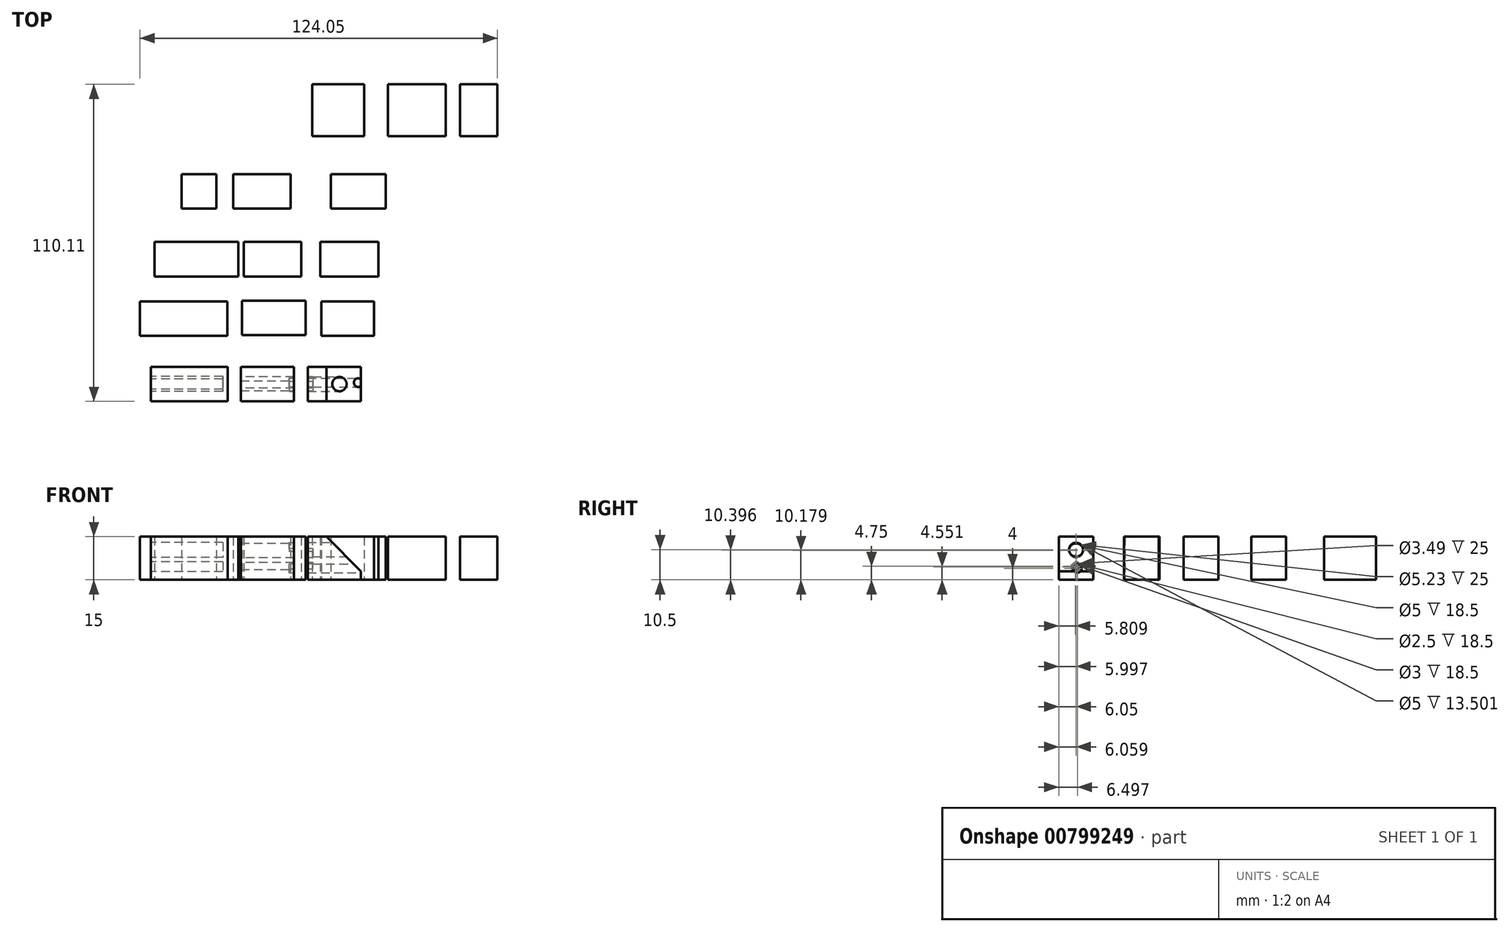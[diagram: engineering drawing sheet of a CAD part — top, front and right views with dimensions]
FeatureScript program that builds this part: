
annotation { "Feature Type Name" : "Feature", "Feature Type Description" : "" }
export const myFeature = defineFeature(function(context is Context, id is Id, definition is map)
    precondition{}
    {
        {
            var Q0;
            Q0=qCreatedBy(makeId("Top.planeOp"),FACE);
            var sketch = newSketch(context, id + "F0", { "sketchPlane" : qUnion([Q0])});
            skLineSegment(sketch, "E0.bottom", {"start": v(-47.12, -60.81) * mm, "end": v(-20.37, -60.81) * mm});
            skLineSegment(sketch, "E0.top", {"start": v(-47.12, -48.81) * mm, "end": v(-20.37, -48.81) * mm});
            skLineSegment(sketch, "E0.left", {"start": v(-47.12, -60.81) * mm, "end": v(-47.12, -48.81) * mm});
            skLineSegment(sketch, "E0.right", {"start": v(-20.37, -60.81) * mm, "end": v(-20.37, -48.81) * mm});
            skLineSegment(sketch, "E1.bottom", {"start": v(-15.87, -60.81) * mm, "end": v(2.63, -60.81) * mm});
            skLineSegment(sketch, "E1.top", {"start": v(-15.87, -48.81) * mm, "end": v(2.63, -48.81) * mm});
            skLineSegment(sketch, "E1.left", {"start": v(-15.87, -60.81) * mm, "end": v(-15.87, -48.81) * mm});
            skLineSegment(sketch, "E1.right", {"start": v(2.63, -60.81) * mm, "end": v(2.63, -48.81) * mm});
            skLineSegment(sketch, "E2.bottom", {"start": v(7.38, -48.81) * mm, "end": v(25.88, -48.81) * mm});
            skLineSegment(sketch, "E2.top", {"start": v(7.38, -60.81) * mm, "end": v(25.88, -60.81) * mm});
            skLineSegment(sketch, "E2.left", {"start": v(7.38, -48.81) * mm, "end": v(7.38, -60.81) * mm});
            skLineSegment(sketch, "E2.right", {"start": v(25.88, -48.81) * mm, "end": v(25.88, -60.81) * mm});
            skLineSegment(sketch, "E3.bottom", {"start": v(-20.54, -38.1) * mm, "end": v(-50.85, -38.1) * mm});
            skLineSegment(sketch, "E3.top", {"start": v(-20.54, -26.1) * mm, "end": v(-50.85, -26.1) * mm});
            skLineSegment(sketch, "E3.left", {"start": v(-20.54, -38.1) * mm, "end": v(-20.54, -26.1) * mm});
            skLineSegment(sketch, "E3.right", {"start": v(-50.85, -38.1) * mm, "end": v(-50.85, -26.1) * mm});
            skLineSegment(sketch, "E4.bottom", {"start": v(-15.44, -37.82) * mm, "end": v(6.66, -37.82) * mm});
            skLineSegment(sketch, "E4.top", {"start": v(-15.44, -25.82) * mm, "end": v(6.66, -25.82) * mm});
            skLineSegment(sketch, "E4.left", {"start": v(-15.44, -37.82) * mm, "end": v(-15.44, -25.82) * mm});
            skLineSegment(sketch, "E4.right", {"start": v(6.66, -37.82) * mm, "end": v(6.66, -25.82) * mm});
            skLineSegment(sketch, "E5.bottom", {"start": v(12.04, -38.1) * mm, "end": v(30.45, -38.1) * mm});
            skLineSegment(sketch, "E5.top", {"start": v(12.04, -26.1) * mm, "end": v(30.45, -26.1) * mm});
            skLineSegment(sketch, "E5.left", {"start": v(12.04, -38.1) * mm, "end": v(12.04, -26.1) * mm});
            skLineSegment(sketch, "E5.right", {"start": v(30.45, -38.1) * mm, "end": v(30.45, -26.1) * mm});
            skLineSegment(sketch, "E6.bottom", {"start": v(-45.75, -17.42) * mm, "end": v(-16.75, -17.42) * mm});
            skLineSegment(sketch, "E6.top", {"start": v(-45.75, -5.42) * mm, "end": v(-16.75, -5.42) * mm});
            skLineSegment(sketch, "E6.left", {"start": v(-45.75, -17.42) * mm, "end": v(-45.75, -5.42) * mm});
            skLineSegment(sketch, "E6.right", {"start": v(-16.75, -17.42) * mm, "end": v(-16.75, -5.42) * mm});
            skLineSegment(sketch, "E7.bottom", {"start": v(-14.87, -17.42) * mm, "end": v(5.13, -17.42) * mm});
            skLineSegment(sketch, "E7.top", {"start": v(-14.87, -5.42) * mm, "end": v(5.13, -5.42) * mm});
            skLineSegment(sketch, "E7.left", {"start": v(-14.87, -17.42) * mm, "end": v(-14.87, -5.42) * mm});
            skLineSegment(sketch, "E7.right", {"start": v(5.13, -17.42) * mm, "end": v(5.13, -5.42) * mm});
            skLineSegment(sketch, "E8.bottom", {"start": v(11.76, -17.42) * mm, "end": v(31.87, -17.42) * mm});
            skLineSegment(sketch, "E8.top", {"start": v(11.76, -5.42) * mm, "end": v(31.87, -5.42) * mm});
            skLineSegment(sketch, "E8.left", {"start": v(11.76, -17.42) * mm, "end": v(11.76, -5.42) * mm});
            skLineSegment(sketch, "E8.right", {"start": v(31.87, -17.42) * mm, "end": v(31.87, -5.42) * mm});
            skLineSegment(sketch, "E9.bottom", {"start": v(15.44, 6.1) * mm, "end": v(34.44, 6.1) * mm});
            skLineSegment(sketch, "E9.top", {"start": v(15.44, 18.1) * mm, "end": v(34.44, 18.1) * mm});
            skLineSegment(sketch, "E9.left", {"start": v(15.44, 6.1) * mm, "end": v(15.44, 18.1) * mm});
            skLineSegment(sketch, "E9.right", {"start": v(34.44, 6.1) * mm, "end": v(34.44, 18.1) * mm});
            skPoint(sketch, "E10.oppositeSnap0", {"position": v(24.94, 18.1) * mm});
            skLineSegment(sketch, "E10.bottom", {"start": v(1.45, 6.1) * mm, "end": v(-18.55, 6.1) * mm});
            skLineSegment(sketch, "E10.top", {"start": v(1.45, 18.1) * mm, "end": v(-18.55, 18.1) * mm});
            skLineSegment(sketch, "E10.left", {"start": v(1.45, 6.1) * mm, "end": v(1.45, 18.1) * mm});
            skLineSegment(sketch, "E10.right", {"start": v(-18.55, 6.1) * mm, "end": v(-18.55, 18.1) * mm});
            skLineSegment(sketch, "E11.bottom", {"start": v(-24.4, 6.1) * mm, "end": v(-36.4, 6.1) * mm});
            skLineSegment(sketch, "E11.top", {"start": v(-24.4, 18.1) * mm, "end": v(-36.4, 18.1) * mm});
            skLineSegment(sketch, "E11.left", {"start": v(-24.4, 6.1) * mm, "end": v(-24.4, 18.1) * mm});
            skLineSegment(sketch, "E11.right", {"start": v(-36.4, 6.1) * mm, "end": v(-36.4, 18.1) * mm});
            skLineSegment(sketch, "E12.bottom", {"start": v(60.2, 31.3) * mm, "end": v(73.2, 31.3) * mm});
            skLineSegment(sketch, "E12.top", {"start": v(60.2, 49.3) * mm, "end": v(73.2, 49.3) * mm});
            skLineSegment(sketch, "E12.left", {"start": v(60.2, 31.3) * mm, "end": v(60.2, 49.3) * mm});
            skLineSegment(sketch, "E12.right", {"start": v(73.2, 31.3) * mm, "end": v(73.2, 49.3) * mm});
            skLineSegment(sketch, "E13.bottom", {"start": v(55.27, 31.3) * mm, "end": v(35.27, 31.3) * mm});
            skLineSegment(sketch, "E13.top", {"start": v(55.27, 49.3) * mm, "end": v(35.27, 49.3) * mm});
            skLineSegment(sketch, "E13.left", {"start": v(55.27, 31.3) * mm, "end": v(55.27, 49.3) * mm});
            skLineSegment(sketch, "E13.right", {"start": v(35.27, 31.3) * mm, "end": v(35.27, 49.3) * mm});
            skLineSegment(sketch, "E14.bottom", {"start": v(26.92, 31.3) * mm, "end": v(8.92, 31.3) * mm});
            skLineSegment(sketch, "E14.top", {"start": v(26.92, 49.3) * mm, "end": v(8.92, 49.3) * mm});
            skLineSegment(sketch, "E14.left", {"start": v(26.92, 31.3) * mm, "end": v(26.92, 49.3) * mm});
            skLineSegment(sketch, "E14.right", {"start": v(8.92, 31.3) * mm, "end": v(8.92, 49.3) * mm});
            skSolve(sketch);
        }
        {
            var Q0;
            Q0 = qSketchRegion(id + "F0", true);
            extrude(context, id + "F1", {"entities" : qUnion([Q0]), "depth" : 15 * mm, "offsetDistance" : 25 * mm});
        }
        {
            var Q0;
            Q0=makeQuery(id+"F1.opExtrude","SWEPT_FACE",FACE,{"disambiguationData":[OSD([sQuery(id+"F0.wireOp",EDGE,"E2.right")])]});
            var sketch = newSketch(context, id + "F2", { "sketchPlane" : qUnion([Q0])});
            skCircle(sketch, "E15", {"center": v(-54.81, 10.5) * mm, "radius": 2.5 * mm});
            skCircle(sketch, "E16", {"center": v(-54.31, 4) * mm, "radius": 1.5 * mm});
            skSolve(sketch);
        }
        {
            var Q0;
            Q0 = qSketchRegion(id + "F2", true);
            extrude(context, id + "F3", {"entities" : qUnion([Q0]), "operationType" : NewBodyOperationType.REMOVE, "oppositeDirection" : true, "depth" : 25 * mm, "offsetDistance" : 25 * mm});
        }
        {
            var Q0;
            Q0=makeQuery(id+"F1.opExtrude","SWEPT_FACE",FACE,{"disambiguationData":[OSD([sQuery(id+"F0.wireOp",EDGE,"E0.left")])]});
            var sketch = newSketch(context, id + "F4", { "sketchPlane" : qUnion([Q0])});
            skCircle(sketch, "E17", {"center": v(54.76, 10.4) * mm, "radius": 2.62 * mm});
            skCircle(sketch, "E18", {"center": v(54.81, 4.55) * mm, "radius": 1.74 * mm});
            skPoint(sketch, "E18.centerSnap0", {"position": v(54.81, 0) * mm});
            skSolve(sketch);
        }
        {
            var Q0;
            Q0 = qSketchRegion(id + "F4", true);
            extrude(context, id + "F5", {"entities" : qUnion([Q0]), "operationType" : NewBodyOperationType.REMOVE, "oppositeDirection" : true, "depth" : 25 * mm, "offsetDistance" : 25 * mm});
        }
        {
            var Q0;
            Q0=makeQuery(id+"F1.opExtrude","SWEPT_FACE",FACE,{"disambiguationData":[OSD([sQuery(id+"F0.wireOp",EDGE,"E1.left")])]});
            var sketch = newSketch(context, id + "F6", { "sketchPlane" : qUnion([Q0])});
            skCircle(sketch, "E19", {"center": v(54.75, 10.18) * mm, "radius": 2.5 * mm});
            skCircle(sketch, "E20", {"center": v(55, 4.75) * mm, "radius": 1.25 * mm});
            skSolve(sketch);
        }
        {
            var Q0;
            Q0 = qSketchRegion(id + "F6", true);
            extrude(context, id + "F7", {"entities" : qUnion([Q0]), "operationType" : NewBodyOperationType.REMOVE, "oppositeDirection" : true, "depth" : 25 * mm, "offsetDistance" : 25 * mm});
        }
        {
            var Q0;
            Q0=makeQuery(id+"F1.opExtrude","CAP_EDGE",EDGE,{"disambiguationData":[OSD([sQuery(id+"F0.wireOp",EDGE,"E2.right")])],"isStart":false});
            chamfer(context, id + "F8", {"entities" : qUnion([Q0]), "width" : 12 * mm, "tangentPropagation" : true});
        }
    });
